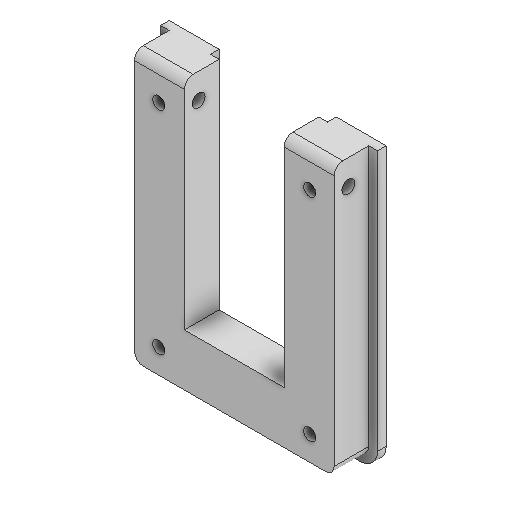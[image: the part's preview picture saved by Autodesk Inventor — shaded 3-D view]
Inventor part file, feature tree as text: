
AUTODESK INVENTOR PART (.ipt)
format: ipt  version: 2022 (Build 260153000, 153)  size: 196,096 bytes
history: native  units: mm
features: sketch x5, extrude x4, projected_geometry x3, fillet x1, hole x1
ambient origin geometry x8: Origin, YZ Plane, XZ Plane, XY Plane, X Axis, Y Axis, Z Axis, Center Point
bodies: Volumenkörper1 (feature_tree)
feature tree (14):
  extrude  "Extrusion1"  Depth=76.0mm
  extrude  "Extrusion2"  Depth=50.0mm
  extrude  "Extrusion3"  Depth=10.0mm
  fillet  "Rundung1"  Radius=10.0mm
  extrude  "Extrusion4"  Depth=25.0mm TaperAngle=0.0deg
  hole  "Bohrung1"  [1 undecoded]
  sketch  "Skizze1"  dims[d0=23.0mm d1=76.0mm]
  sketch  "Skizze2"  dims[d2=12.0mm d3=50.0mm]
  sketch  "Skizze3"  dims[d4=50.0mm d5=46.0mm d6=10.0mm d7=0.0mm]
  projected_geometry  "Projizierte Kontur1"
  sketch  "Skizze4"  dims[d8=0.5mm d9=25.0mm d10=0.0mm]
  projected_geometry  "Projizierte Kontur2"
  sketch  "Skizze5"  dims[d11=3.0mm d12=10.0mm d13=0.0mm d14=2.0mm d15=2.0mm d16=2.0mm d17=0.0mm d18=2.0mm d19=2.0mm d20=0.0mm d21=2.8mm d22=6.0mm d23=4.0mm d24=2.0mm d25=90.0deg d26=12.0mm d27=20.594885mm]
  projected_geometry  "Projizierte Kontur3"
note: 1 required parameter value undecoded (feature->parameter linkage not recoverable at this tier; creation-order binding heuristic only, values carry confidence <= 0.55)
